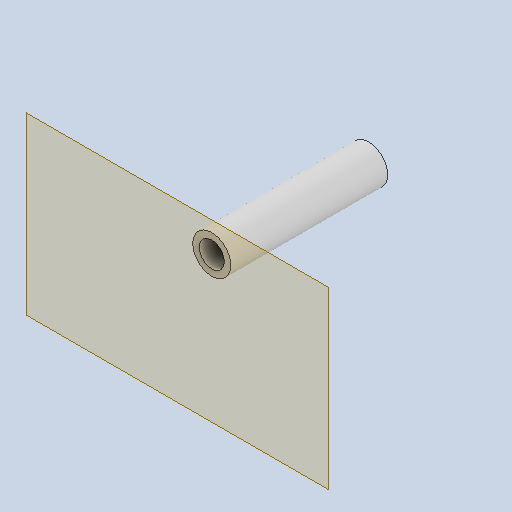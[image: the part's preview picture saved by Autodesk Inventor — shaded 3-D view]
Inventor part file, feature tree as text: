
AUTODESK INVENTOR PART (.ipt)
format: ipt  version: 2023 (Build 270158000, 158)  size: 243,200 bytes
history: native  units: mm
features: other x4, plane x2, sketch x1, extrude x1, reference x1
ambient origin geometry x8: Origin, YZ Plane, XZ Plane, XY Plane, X Axis, Y Axis, Z Axis, Center Point
bodies: Solid1 (feature_tree)
feature tree (9):
  plane  "Work Plane1"
  sketch  "Sketch1"  dims[d0=0.3mm d1=2.0mm d2=10.0mm d3=0.0mm]
  plane  "Work Plane2"
  extrude  "Extrusion1"  Depth=10.0mm
  reference  "Reference1"
  parser-record x1  (decoder bookkeeping rows leaked as tree rows — omitted from the tree; the rows remain in map.json)
  other  "doorLockAssembly_V3.iam"
  other  "gear_V3:1"
  other  "tempMotorHolder_V3:1"
note: 1 file-system path scrubbed to <path> (originals preserved in map.json)
